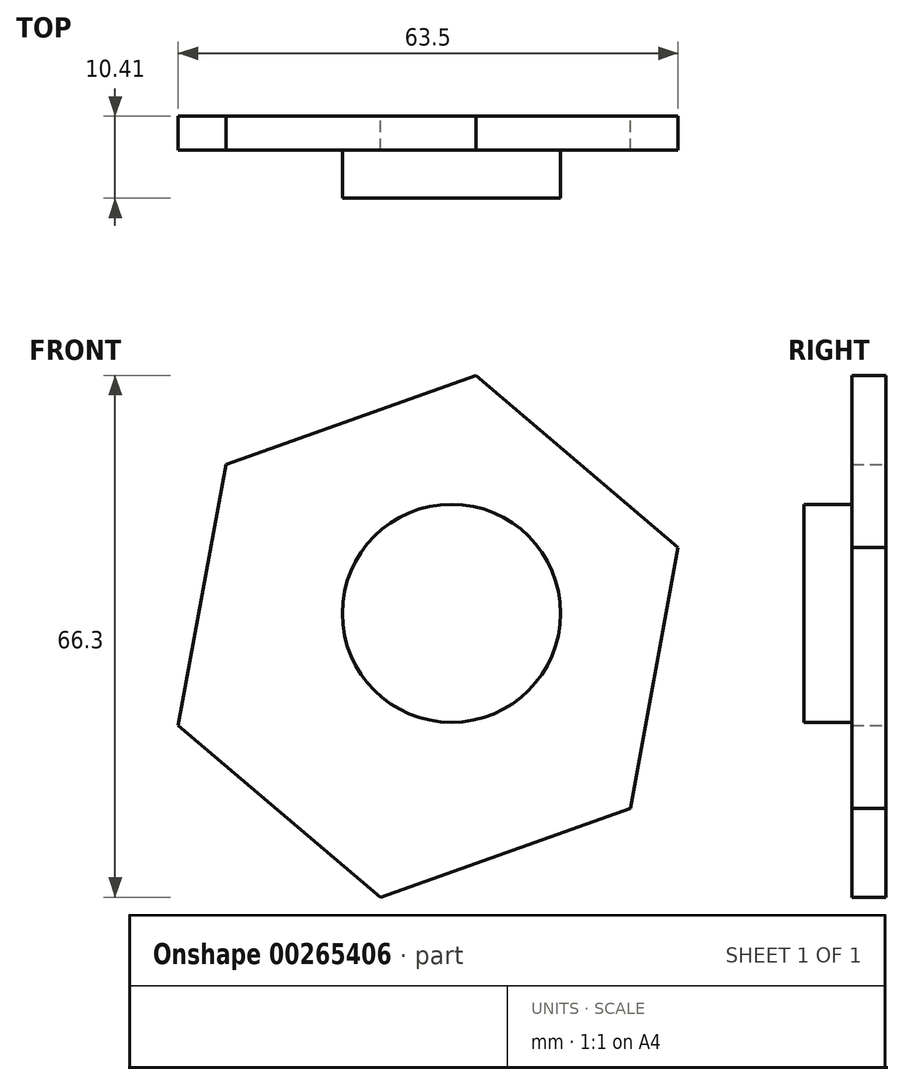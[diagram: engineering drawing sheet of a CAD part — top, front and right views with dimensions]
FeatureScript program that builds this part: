
annotation { "Feature Type Name" : "Feature", "Feature Type Description" : "" }
export const myFeature = defineFeature(function(context is Context, id is Id, definition is map)
    precondition{}
    {
        {
            var Q0;
            Q0=qCreatedBy(makeId("Front.planeOp"),FACE);
            var sketch = newSketch(context, id + "F0", { "sketchPlane" : qUnion([Q0])});
            skCircle(sketch, "E0.cCircle", {"center": v(0, 0) * mm, "radius": 29.19 * mm, "construction": true});
            skLineSegment(sketch, "E0.0", {"start": v(-25.67, 21.84) * mm, "end": v(6.08, 33.15) * mm});
            skLineSegment(sketch, "E0.1", {"start": v(6.08, 33.15) * mm, "end": v(31.75, 11.31) * mm});
            skLineSegment(sketch, "E0.2", {"start": v(31.75, 11.31) * mm, "end": v(25.67, -21.84) * mm});
            skLineSegment(sketch, "E0.3", {"start": v(25.67, -21.84) * mm, "end": v(-6.08, -33.15) * mm});
            skLineSegment(sketch, "E0.4", {"start": v(-6.08, -33.15) * mm, "end": v(-31.75, -11.31) * mm});
            skLineSegment(sketch, "E0.5", {"start": v(-31.75, -11.31) * mm, "end": v(-25.67, 21.84) * mm});
            skPoint(sketch, "E0.0.midPoint", {"position": v(-9.8, 27.5) * mm});
            skCircle(sketch, "E1", {"center": v(0, 0) * mm, "radius": 16.85 * mm});
            skLineSegment(sketch, "E2", {"start": v(0, 0) * mm, "end": v(6.08, 33.15) * mm});
            skLineSegment(sketch, "E3", {"start": v(0, 0) * mm, "end": v(-25.67, 21.84) * mm});
            skLineSegment(sketch, "E4", {"start": v(0, 0) * mm, "end": v(-31.75, -11.31) * mm});
            skLineSegment(sketch, "E5", {"start": v(0, 0) * mm, "end": v(-6.08, -33.15) * mm});
            skLineSegment(sketch, "E6", {"start": v(0, 0) * mm, "end": v(31.75, 11.31) * mm});
            skLineSegment(sketch, "E7", {"start": v(-25.67, 21.84) * mm, "end": v(-15.87, -5.66) * mm});
            skSolve(sketch);
        }
        {
            var Q0;
            {var subQ0=sQuery(id+"F0.wireOp",EDGE,"E0.0");Q0=makeQuery(id+"F0.imprint","IMPRINT",FACE,{"disambiguationData":[TD([[makeQuery(id+"F0.imprint","IMPRINT",EDGE,{"derivedFrom":subQ0}),-1.0]])]});}
            var Q1;
            {var subQ0=sQuery(id+"F0.wireOp",EDGE,"E0.5");Q1=makeQuery(id+"F0.imprint","IMPRINT",FACE,{"disambiguationData":[TD([[makeQuery(id+"F0.imprint","IMPRINT",EDGE,{"derivedFrom":subQ0}),-1.0]])]});}
            var Q2;
            {var subQ0=sQuery(id+"F0.wireOp",EDGE,"E0.1");Q2=makeQuery(id+"F0.imprint","IMPRINT",FACE,{"disambiguationData":[TD([[makeQuery(id+"F0.imprint","IMPRINT",EDGE,{"derivedFrom":subQ0}),-1.0]])]});}
            var Q3;
            {var subQ6=sQuery(id+"F0.wireOp",EDGE,"E0.2");Q3=makeQuery(id+"F0.imprint","IMPRINT",FACE,{"disambiguationData":[TD([[makeQuery(id+"F0.imprint","IMPRINT",EDGE,{"derivedFrom":subQ6}),-1.0]])]});}
            var Q4;
            {var subQ0=sQuery(id+"F0.wireOp",EDGE,"E0.4");Q4=makeQuery(id+"F0.imprint","IMPRINT",FACE,{"disambiguationData":[TD([[makeQuery(id+"F0.imprint","IMPRINT",EDGE,{"derivedFrom":subQ0}),-1.0]])]});}
            var Q5;
            {var subQ0=sQuery(id+"F0.wireOp",EDGE,"E2");var subQ1=sQuery(id+"F0.wireOp",EDGE,"E1");var subQ2=makeQuery(id+"F0.imprint","INTERSECT",VERTEX,{"derivedFrom":[subQ1,subQ0]});Q5=makeQuery(id+"F0.imprint","IMPRINT",FACE,{"disambiguationData":[TD([[makeQuery(id+"F0.imprint","IMPRINT",EDGE,{"disambiguationData":[TD([[subQ2,1.0]])],"derivedFrom":subQ1}),1.0]])]});}
            var Q6;
            {var subQ0=sQuery(id+"F0.wireOp",EDGE,"E2");var subQ1=sQuery(id+"F0.wireOp",EDGE,"E1");var subQ2=makeQuery(id+"F0.imprint","INTERSECT",VERTEX,{"derivedFrom":[subQ1,subQ0]});Q6=makeQuery(id+"F0.imprint","IMPRINT",FACE,{"disambiguationData":[TD([[makeQuery(id+"F0.imprint","IMPRINT",EDGE,{"disambiguationData":[TD([[subQ2,-1.0]])],"derivedFrom":subQ1}),1.0]])]});}
            var Q7;
            {var subQ1=sQuery(id+"F0.wireOp",EDGE,"E1");var subQ3=sQuery(id+"F0.wireOp",EDGE,"E3");var subQ4=makeQuery(id+"F0.imprint","INTERSECT",VERTEX,{"derivedFrom":[subQ1,subQ3]});Q7=makeQuery(id+"F0.imprint","IMPRINT",FACE,{"disambiguationData":[TD([[makeQuery(id+"F0.imprint","IMPRINT",EDGE,{"disambiguationData":[TD([[subQ4,-1.0]])],"derivedFrom":subQ1}),1.0]])]});}
            var Q8;
            {var subQ0=sQuery(id+"F0.wireOp",EDGE,"E7");Q8=makeQuery(id+"F0.imprint","IMPRINT",FACE,{"disambiguationData":[TD([[makeQuery(id+"F0.imprint","IMPRINT",EDGE,{"derivedFrom":subQ0}),1.0]])]});}
            var Q9;
            {var subQ1=sQuery(id+"F0.wireOp",EDGE,"E1");var subQ3=sQuery(id+"F0.wireOp",EDGE,"E5");var subQ4=makeQuery(id+"F0.imprint","INTERSECT",VERTEX,{"derivedFrom":[subQ1,subQ3]});Q9=makeQuery(id+"F0.imprint","IMPRINT",FACE,{"disambiguationData":[TD([[makeQuery(id+"F0.imprint","IMPRINT",EDGE,{"disambiguationData":[TD([[subQ4,1.0]])],"derivedFrom":subQ1}),1.0]])]});}
            var Q10;
            {var subQ0=sQuery(id+"F0.wireOp",EDGE,"E6");var subQ1=sQuery(id+"F0.wireOp",EDGE,"E1");var subQ2=makeQuery(id+"F0.imprint","INTERSECT",VERTEX,{"derivedFrom":[subQ1,subQ0]});Q10=makeQuery(id+"F0.imprint","IMPRINT",FACE,{"disambiguationData":[TD([[makeQuery(id+"F0.imprint","IMPRINT",EDGE,{"disambiguationData":[TD([[subQ2,1.0]])],"derivedFrom":subQ1}),1.0]])]});}
            extrude(context, id + "F1", {"entities" : qUnion([Q0, Q1, Q2, Q3, Q4, Q5, Q6, Q7, Q8, Q9, Q10]), "depth" : 4.32 * mm});
        }
        {
            var Q0;
            Q0=makeQuery(id+"F1.opExtrude","CAP_FACE",FACE,{"disambiguationData":[OSD([sQuery(id+"F0.wireOp",EDGE,"E0.0"),sQuery(id+"F0.wireOp",EDGE,"E0.1"),sQuery(id+"F0.wireOp",EDGE,"E0.2"),sQuery(id+"F0.wireOp",EDGE,"E0.3"),sQuery(id+"F0.wireOp",EDGE,"E0.4"),sQuery(id+"F0.wireOp",EDGE,"E0.5")])],"isStart":false});
            var sketch = newSketch(context, id + "F2", { "sketchPlane" : qUnion([Q0])});
            skCircle(sketch, "E8", {"center": v(2.95, 2.92) * mm, "radius": 13.85 * mm});
            skSolve(sketch);
        }
        {
            var Q0;
            Q0=makeQuery(id+"F2.imprint","IMPRINT",FACE,{"disambiguationData":[TD([[makeQuery(id+"F2.imprint","IMPRINT",EDGE,{"derivedFrom":sQuery(id+"F2.wireOp",EDGE,"E8")}),1.0]])]});
            extrude(context, id + "F3", {"entities" : qUnion([Q0]), "operationType" : NewBodyOperationType.ADD, "depth" : 6.1 * mm});
        }
    });
